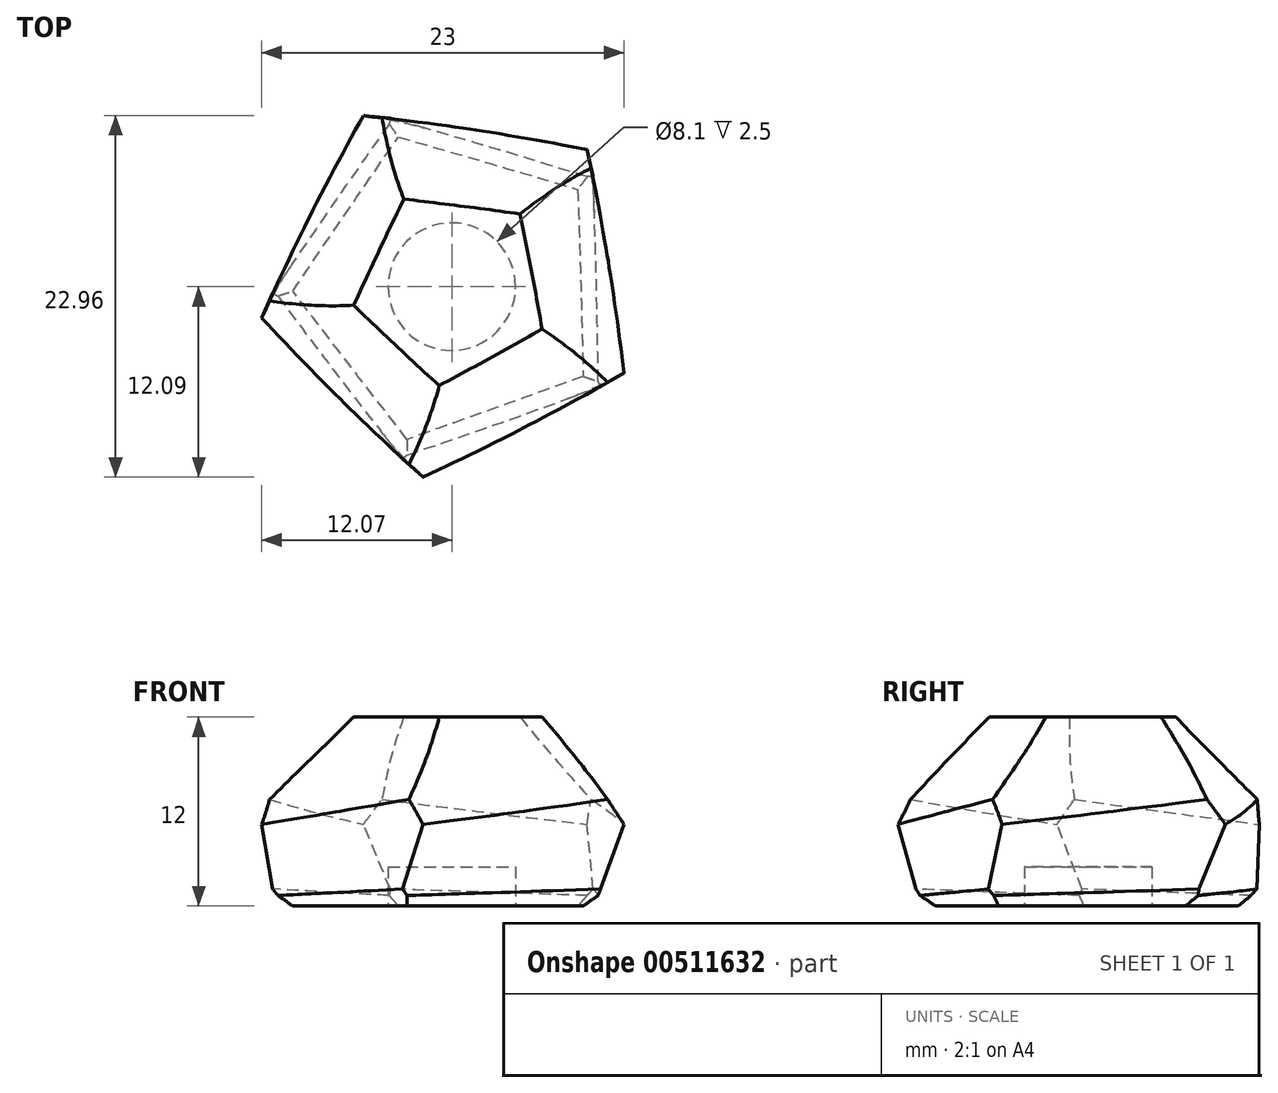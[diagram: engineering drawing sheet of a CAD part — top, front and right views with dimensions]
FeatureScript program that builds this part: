
annotation { "Feature Type Name" : "Feature", "Feature Type Description" : "" }
export const myFeature = defineFeature(function(context is Context, id is Id, definition is map)
    precondition{}
    {
        {
            var Q0;
            Q0=qCreatedBy(makeId("Top.planeOp"),FACE);
            var sketch = newSketch(context, id + "F0", { "sketchPlane" : qUnion([Q0])});
            skCircle(sketch, "E0.cCircle", {"center": v(0, 0) * mm, "radius": 9.06 * mm, "construction": true});
            skLineSegment(sketch, "E0.0", {"start": v(9.06, 6.58) * mm, "end": v(9.06, -6.58) * mm});
            skLineSegment(sketch, "E0.1", {"start": v(9.06, -6.58) * mm, "end": v(-3.46, -10.65) * mm});
            skLineSegment(sketch, "E0.2", {"start": v(-3.46, -10.65) * mm, "end": v(-11.2, 0) * mm});
            skLineSegment(sketch, "E0.3", {"start": v(-11.2, 0) * mm, "end": v(-3.46, 10.65) * mm});
            skLineSegment(sketch, "E0.4", {"start": v(-3.46, 10.65) * mm, "end": v(9.06, 6.58) * mm});
            skPoint(sketch, "E0.0.midPoint", {"position": v(9.06, 0) * mm});
            skSolve(sketch);
        }
        {
            var Q0;
            Q0=qCreatedBy(makeId("Top.planeOp"),FACE);
            cPlane(context, id + "F1", {"entities" : qUnion([Q0]), "cplaneType" : CPlaneType.OFFSET, "offset" : 12 * mm, "width" : 150 * mm, "height" : 150 * mm});
        }
        {
            var Q0;
            Q0=qCreatedBy(id+"F1.planeOp",FACE);
            var sketch = newSketch(context, id + "F2", { "sketchPlane" : qUnion([Q0])});
            skCircle(sketch, "E1.cCircle", {"center": v(0, 0) * mm, "radius": 11.33 * mm, "construction": true});
            skLineSegment(sketch, "E1.0", {"start": v(8, 11.5) * mm, "end": v(13.4, -4.05) * mm});
            skLineSegment(sketch, "E1.1", {"start": v(13.4, -4.05) * mm, "end": v(0.29, -14) * mm});
            skLineSegment(sketch, "E1.2", {"start": v(0.29, -14) * mm, "end": v(-13.22, -4.6) * mm});
            skLineSegment(sketch, "E1.3", {"start": v(-13.22, -4.6) * mm, "end": v(-8.46, 11.15) * mm});
            skLineSegment(sketch, "E1.4", {"start": v(-8.46, 11.15) * mm, "end": v(8, 11.5) * mm});
            skPoint(sketch, "E1.0.midPoint", {"position": v(10.7, 3.72) * mm});
            skPoint(sketch, "E2.0", {"position": v(-11.2, 0) * mm});
            skSolve(sketch);
        }
        {
            var Q0;
            Q0=makeQuery(id+"F0.imprint","IMPRINT",FACE,{"disambiguationData":[TD([[makeQuery(id+"F0.imprint","IMPRINT",EDGE,{"derivedFrom":sQuery(id+"F0.wireOp",EDGE,"E0.0")}),-1.0]])]});
            var Q1;
            Q1=makeQuery(id+"F2.imprint","IMPRINT",FACE,{"disambiguationData":[TD([[makeQuery(id+"F2.imprint","IMPRINT",EDGE,{"derivedFrom":sQuery(id+"F2.wireOp",EDGE,"E1.0")}),-1.0]])]});
            loft(context, id + "F3", {"sheetProfilesArray" : [{ "sheetProfileEntities" : qUnion([Q0]) }, { "sheetProfileEntities" : qUnion([Q1]) }]});
        }
        {
            var Q0;
            Q0=makeQuery(id+"F3.opLoft","CAP_FACE",FACE,{"disambiguationData":[OSD([makeQuery(id+"F0.imprint","IMPRINT",FACE,{"disambiguationData":[TD([[makeQuery(id+"F0.imprint","IMPRINT",EDGE,{"derivedFrom":sQuery(id+"F0.wireOp",EDGE,"E0.0")}),-1.0]])]})])],"isStart":true});
            var sketch = newSketch(context, id + "F4", { "sketchPlane" : qUnion([Q0])});
            skCircle(sketch, "E3", {"center": v(0, 0) * mm, "radius": 4.05 * mm});
            skSolve(sketch);
        }
        {
            var Q0;
            Q0=makeQuery(id+"F4.imprint","IMPRINT",FACE,{"disambiguationData":[TD([[makeQuery(id+"F4.imprint","IMPRINT",EDGE,{"derivedFrom":sQuery(id+"F4.wireOp",EDGE,"E3")}),1.0]])]});
            extrude(context, id + "F5", {"entities" : qUnion([Q0]), "operationType" : NewBodyOperationType.REMOVE, "oppositeDirection" : true, "depth" : 2.5 * mm});
        }
        {
            var Q0;
            Q0=makeQuery(id+"F3.opLoft","MID_CAP_EDGE",EDGE,{"disambiguationData":[OSD([sQuery(id+"F0.wireOp",EDGE,"E0.1"),sQuery(id+"F0.wireOp",EDGE,"E0.2"),sQuery(id+"F0.wireOp",EDGE,"E0.3")])],"capPos":0.0});
            var Q1;
            Q1=makeQuery(id+"F3.opLoft","MID_CAP_EDGE",EDGE,{"disambiguationData":[OSD([sQuery(id+"F0.wireOp",EDGE,"E0.0"),sQuery(id+"F0.wireOp",EDGE,"E0.1"),sQuery(id+"F0.wireOp",EDGE,"E0.2")])],"capPos":0.0});
            var Q2;
            Q2=makeQuery(id+"F3.opLoft","MID_CAP_EDGE",EDGE,{"disambiguationData":[OSD([sQuery(id+"F0.wireOp",EDGE,"E0.0"),sQuery(id+"F0.wireOp",EDGE,"E0.1"),sQuery(id+"F0.wireOp",EDGE,"E0.4")])],"capPos":0.0});
            var Q3;
            Q3=makeQuery(id+"F3.opLoft","MID_CAP_EDGE",EDGE,{"disambiguationData":[OSD([sQuery(id+"F0.wireOp",EDGE,"E0.0"),sQuery(id+"F0.wireOp",EDGE,"E0.3"),sQuery(id+"F0.wireOp",EDGE,"E0.4")])],"capPos":0.0});
            var Q4;
            Q4=makeQuery(id+"F3.opLoft","MID_CAP_EDGE",EDGE,{"disambiguationData":[OSD([sQuery(id+"F0.wireOp",EDGE,"E0.2"),sQuery(id+"F0.wireOp",EDGE,"E0.3"),sQuery(id+"F0.wireOp",EDGE,"E0.4")])],"capPos":0.0});
            chamfer(context, id + "F6", {"entities" : qUnion([Q0, Q1, Q2, Q3, Q4]), "width" : 1 * mm, "tangentPropagation" : true});
        }
        {
            var Q0;
            Q0=makeQuery(id+"F3.opLoft","CAP_FACE",FACE,{"disambiguationData":[OSD([makeQuery(id+"F2.imprint","IMPRINT",FACE,{"disambiguationData":[TD([[makeQuery(id+"F2.imprint","IMPRINT",EDGE,{"derivedFrom":sQuery(id+"F2.wireOp",EDGE,"E1.0")}),-1.0]])]})])],"isStart":true});
            chamfer(context, id + "F7", {"entities" : qUnion([Q0]), "width" : 5 * mm, "tangentPropagation" : true});
        }
    });
